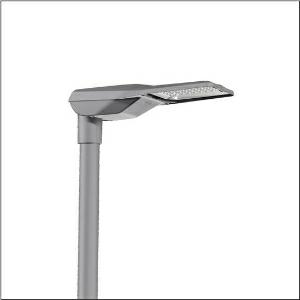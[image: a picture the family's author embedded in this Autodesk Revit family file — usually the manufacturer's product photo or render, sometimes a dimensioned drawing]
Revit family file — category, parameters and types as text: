
# Revit family: streetlight_sl_21_iq_mini___st1_5a_5xe2p41d08hb_72ee
name_source: partatom
category: Lighting Fixtures
units: mm (PartAtom-declared; Revit-internal decimal feet)

## family parameters
Cut with Voids When Loaded = No
Host = Face
Light Source = No
Part Type = Normal
Room Calculation Point = No
Round Connector Dimension = Use Diameter
Shared = No

## types (1)
- --- (1 x LED, 9690 lm, 70.9 W, 4000K)
    Apparent Load = 71 VA
    CIE Flux Codes = 22 53 95 100 100
    Color Rendering = 70
    Color Temperature = 4000K
    Default Elevation = 1800 mm
    Description = Streetlight SL 21 iQ mini, mast luminaire, primary light control with lens, of PMMA, primary optical cover: cover, of toughened safety glass, transparent, light distribution: ST1.5a, light emission: direct distribution, primary light characteristic: asymmetric, installation type: post-top, side-entry, LED, High Power LED, rated luminous flux: 9.690lm, luminous efficacy: 137lm/W, light colour: 740, colour temperature: 4000K, control gear: iQ-Comfort, control: Auto-Match, Temp-Guard, Lumen-Switch, Night-Set, Smart-Wire, Light-Fading, Desk-Remote (wireless, voltage-free reading and setting of iQ features in the workshop via application-optimized NFC function/RFID function), optimised constant luminous flux control (CLO 2.0), pre-setting: linear dimming characteristic, mains connection: 220..240V, AC, 50/60Hz, start of lifetime: 71W, end of service life: 75W, reduction: 31W, luminaire housing, of diecast aluminium, powder-coated, Siteco® metallic grey (DB 702S), corrosivity category C5 mid according to DIN EN ISO 12944, please order mast flange separately, inclination adjustable: 0°, 5°, 10°, 15°, sealing non-destructively replaceable, multi-level sealing system, length: 628mm, width: 235mm, height: 110mm, mast flange for spigot size: 42mm (side-entry): 5XC10008XM4, 60/48mm (side-entry/post-top): 5XC10108XM2, 76/60mm (side-entry/post-top): 5XC10108XM1, mounting height: 4..8m, protection rating (complete): IP66, insulation class (complete): insulation class II (safety insulation), certification: CE, ENEC, ENEC+, VDE, impact resistance: IK10, permissible operating ambient temperature for outdoor applications: -40..+50°C, standard-compliant lighting for roads and squares, packaging unit: 1 piece

Light Distribution: ST1.5a
    Height = 110 mm
    Lamp = 1 x LED
    Lamp Light Flux = 9690 lm
    Lamp Power = 70.9 W
    Lamp count = 1
    Length = 625 mm
    Luminous efficacy = 137 lm/W
    Manufacturer = Siteco
    ModVariant = No
    Model = 5XE2P41D08HB
    Number of Poles = 1
    OnlyDefault = Yes
    Power Factor = 1
    Product Name = Streetlight SL 21 iQ mini | ST1.5a
    Product group = mast luminaire | pylon top
    ProductGroupID = 6100
    Protection Class = Protection class II
    Protection Degree = IP 66
    RLX_Detail_Level = 1
    RLX_Emergency_Light_Flux = 0 lm
    RLX_Emergency_Type = 0
    RLX_Emergency_Type_DB = No
    RlxData = <blob elided: 29825 chars, md5=c1b1f04f>
    Socket = socket
    Standby Power = 0 W
    System Light Flux = 9690 lm
    System Power = 71 W
    Type Comments = factory setting: luminous flux: 100 % | dim-lin: 254 | 711 mA
    Type Image = l_1003519.jpg
    URL = http://relux.com
    VarID = @adj_178489
    Voltage = 0 V
    Weight = 0.00 kg
    Width = 234 mm

## geometry (parser evidence)
native form markers: Blend x4, Sweep x9
no freeform markers — native parametric forms only
